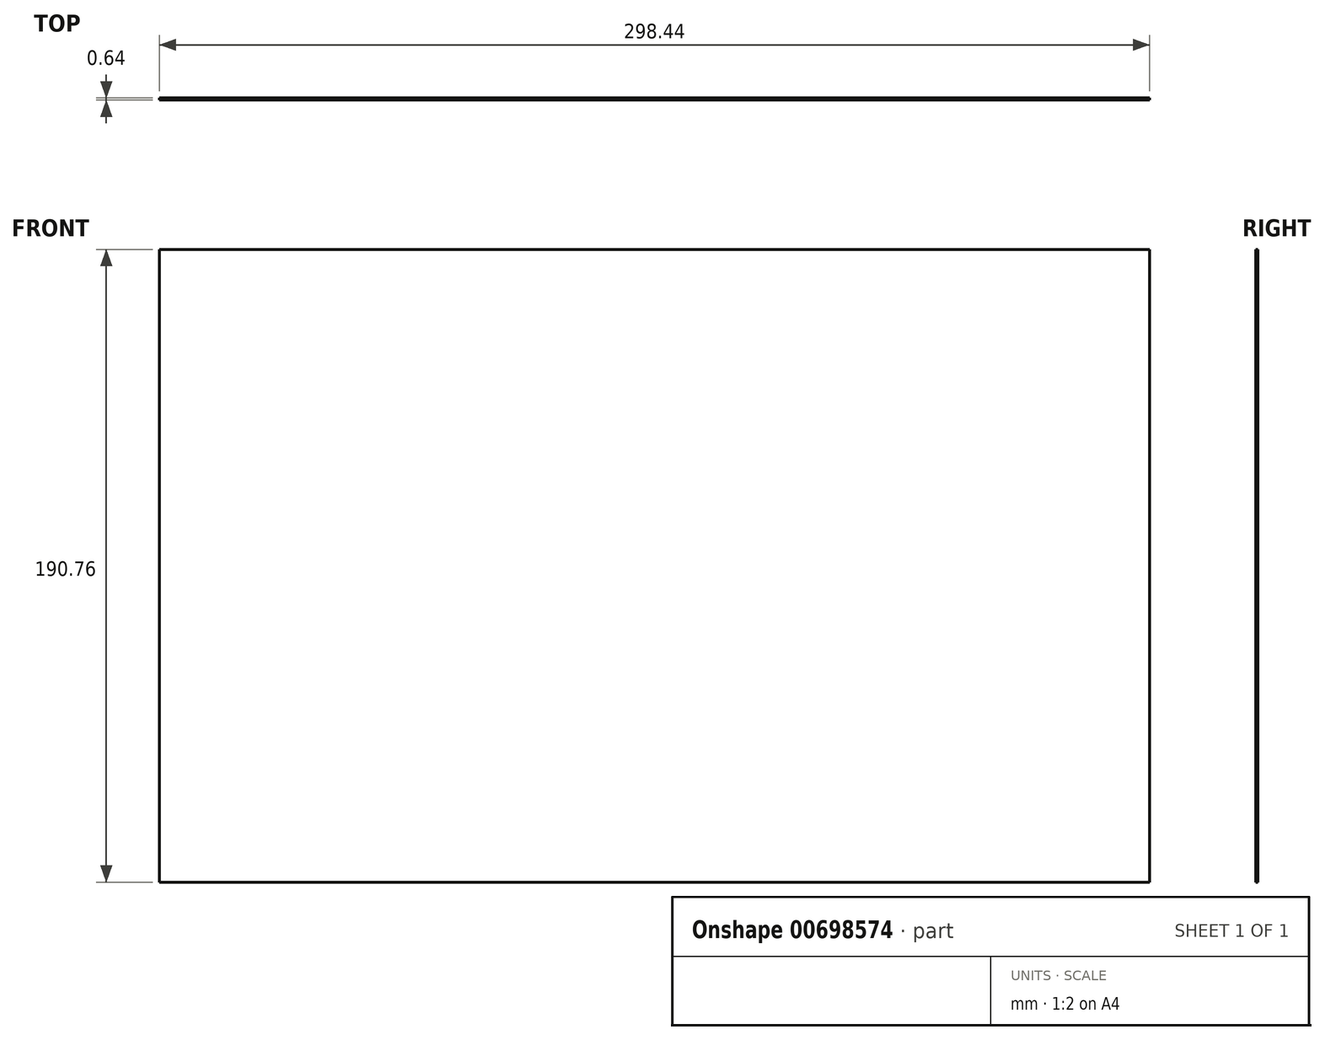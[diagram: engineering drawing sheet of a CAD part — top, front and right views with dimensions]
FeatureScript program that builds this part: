
annotation { "Feature Type Name" : "Feature", "Feature Type Description" : "" }
export const myFeature = defineFeature(function(context is Context, id is Id, definition is map)
    precondition{}
    {
        {
            var Q0;
            Q0=qCreatedBy(makeId("Front.planeOp"),FACE);
            var sketch = newSketch(context, id + "F0", { "sketchPlane" : qUnion([Q0])});
            skLineSegment(sketch, "E0.bottom", {"start": v(149.23, -95.38) * mm, "end": v(-149.23, -95.38) * mm});
            skLineSegment(sketch, "E0.top", {"start": v(149.23, 95.38) * mm, "end": v(-149.23, 95.38) * mm});
            skLineSegment(sketch, "E0.left", {"start": v(149.23, -95.38) * mm, "end": v(149.23, 95.38) * mm});
            skLineSegment(sketch, "E0.right", {"start": v(-149.23, -95.38) * mm, "end": v(-149.23, 95.38) * mm});
            skPoint(sketch, "E0.middle", {"position": v(0, 0) * mm});
            skSolve(sketch);
        }
        {
            var Q0;
            Q0 = qSketchRegion(id + "F0", true);
            extrude(context, id + "F1", {"entities" : qUnion([Q0]), "depth" : 0.64 * mm, "offsetDistance" : 25.4 * mm});
        }
    });
